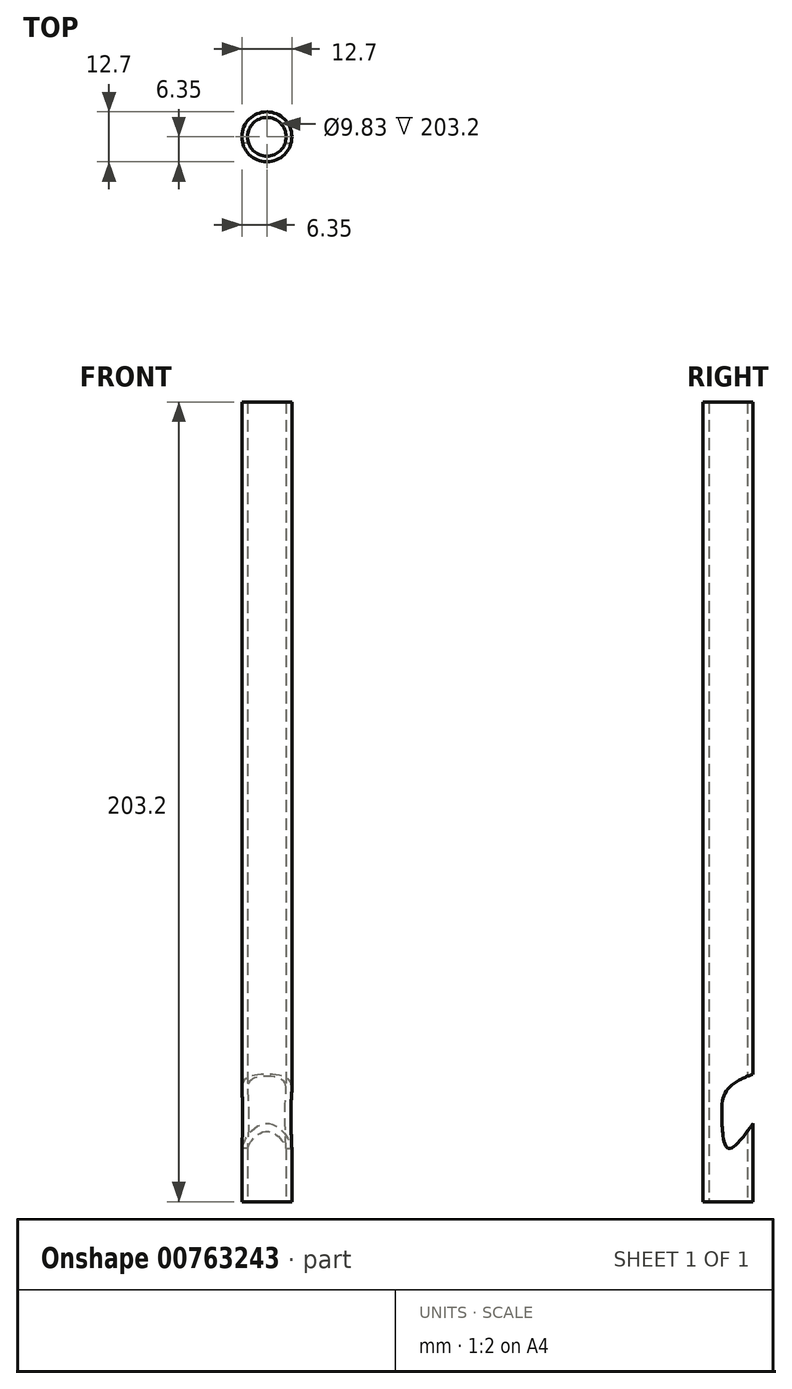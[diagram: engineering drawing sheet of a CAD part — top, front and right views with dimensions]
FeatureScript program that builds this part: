
annotation { "Feature Type Name" : "Feature", "Feature Type Description" : "" }
export const myFeature = defineFeature(function(context is Context, id is Id, definition is map)
    precondition{}
    {
        {
            var Q0;
            Q0=qCreatedBy(makeId("Top.planeOp"),FACE);
            var sketch = newSketch(context, id + "F0", { "sketchPlane" : qUnion([Q0])});
            skCircle(sketch, "E0", {"center": v(0, 0) * mm, "radius": 6.35 * mm});
            skCircle(sketch, "E1", {"center": v(0, 0) * mm, "radius": 4.91 * mm});
            skSolve(sketch);
        }
        {
            var Q0;
            Q0=makeQuery(id+"F0.imprint","IMPRINT",FACE,{"disambiguationData":[TD([[makeQuery(id+"F0.imprint","IMPRINT",EDGE,{"derivedFrom":sQuery(id+"F0.wireOp",EDGE,"E0")}),1.0]])]});
            extrude(context, id + "F1", {"entities" : qUnion([Q0]), "depth" : 203.2 * mm, "offsetDistance" : 25.4 * mm});
        }
        {
            var Q0;
            Q0=qCreatedBy(makeId("Right.planeOp"),FACE);
            cPlane(context, id + "F2", {"entities" : qUnion([Q0]), "cplaneType" : CPlaneType.OFFSET, "offset" : 25.4 * mm, "width" : 152.4 * mm, "height" : 152.4 * mm});
        }
        {
            var Q0;
            Q0=qCreatedBy(id+"F2.planeOp",FACE);
            var sketch = newSketch(context, id + "F3", { "sketchPlane" : qUnion([Q0])});
            skFitSpline(sketch, "E2", {"points": [v(12.24, 32.71) * mm, v(0.94, 29.58) * mm, v(-1.57, 21.42) * mm, v(0, 13.58) * mm, v(7.84, 22.05) * mm, v(12.24, 32.71) * mm]});
            skSolve(sketch);
        }
        {
            var Q0;
            Q0=makeQuery(id+"F3.imprint","IMPRINT",FACE,{"disambiguationData":[TD([[makeQuery(id+"F3.imprint","IMPRINT",EDGE,{"derivedFrom":sQuery(id+"F3.wireOp",EDGE,"E2")}),1.0]])]});
            extrude(context, id + "F4", {"entities" : qUnion([Q0]), "operationType" : NewBodyOperationType.REMOVE, "oppositeDirection" : true, "depth" : 47 * mm, "offsetDistance" : 25.4 * mm});
        }
    });
